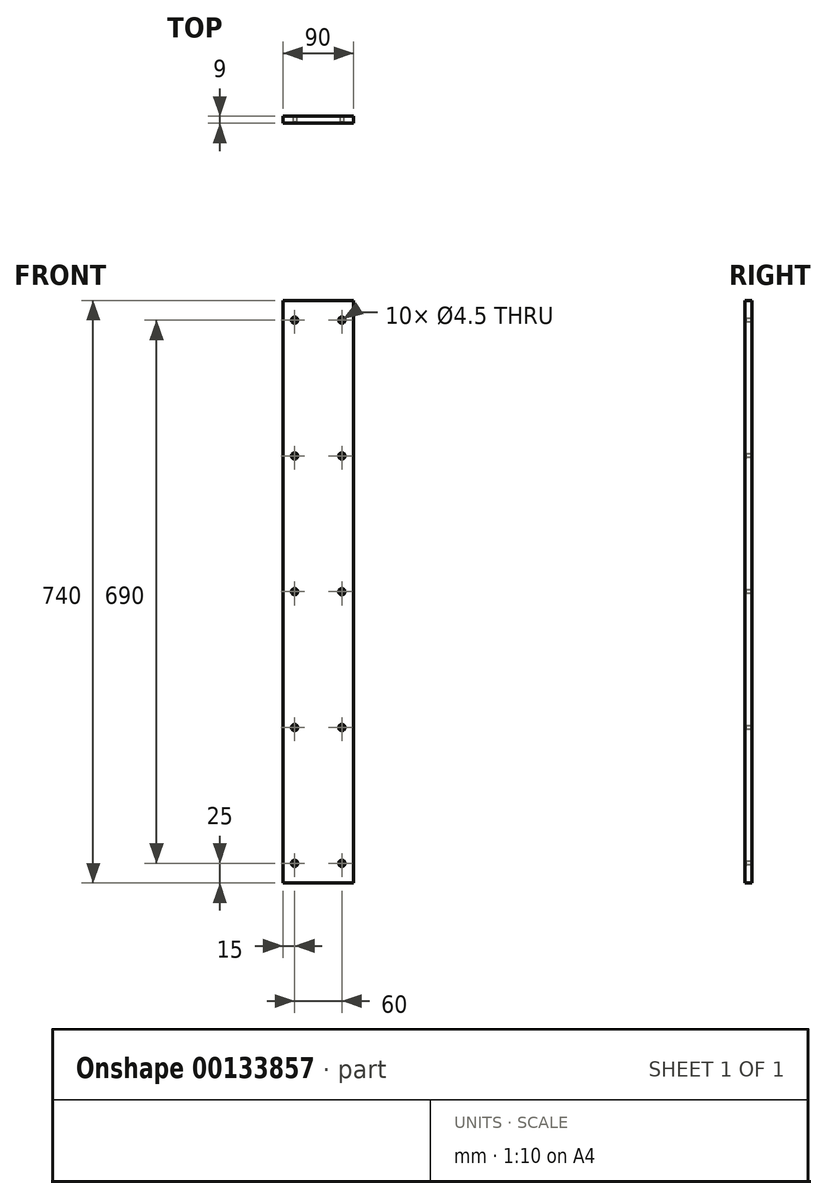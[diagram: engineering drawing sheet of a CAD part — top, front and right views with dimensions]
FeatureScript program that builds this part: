
annotation { "Feature Type Name" : "Feature", "Feature Type Description" : "" }
export const myFeature = defineFeature(function(context is Context, id is Id, definition is map)
    precondition{}
    {
        {
            var Q0;
            Q0=qCreatedBy(makeId("Top.planeOp"),FACE);
            var sketch = newSketch(context, id + "F0", { "sketchPlane" : qUnion([Q0])});
            skLineSegment(sketch, "E0.bottom", {"start": v(45, -4.5) * mm, "end": v(-45, -4.5) * mm});
            skLineSegment(sketch, "E0.top", {"start": v(45, 4.5) * mm, "end": v(-45, 4.5) * mm});
            skLineSegment(sketch, "E0.left", {"start": v(45, -4.5) * mm, "end": v(45, 4.5) * mm});
            skLineSegment(sketch, "E0.right", {"start": v(-45, -4.5) * mm, "end": v(-45, 4.5) * mm});
            skPoint(sketch, "E0.middle", {"position": v(0, 0) * mm});
            skSolve(sketch);
        }
        {
            var Q0;
            Q0=makeQuery(id+"F0.imprint","IMPRINT",FACE,{"disambiguationData":[TD([[makeQuery(id+"F0.imprint","IMPRINT",EDGE,{"derivedFrom":sQuery(id+"F0.wireOp",EDGE,"E0.bottom")}),-1.0]])]});
            extrude(context, id + "F1", {"entities" : qUnion([Q0]), "oppositeDirection" : true, "depth" : 740 * mm});
        }
        {
            var Q0;
            Q0=makeQuery(id+"F1.opExtrude","SWEPT_FACE",FACE,{"disambiguationData":[OSD([sQuery(id+"F0.wireOp",EDGE,"E0.bottom")])]});
            var sketch = newSketch(context, id + "F2", { "sketchPlane" : qUnion([Q0])});
            skPoint(sketch, "E1", {"position": v(-30, -25) * mm});
            skPoint(sketch, "E2", {"position": v(-30, -197.5) * mm});
            skPoint(sketch, "E3", {"position": v(-30, -370) * mm});
            skPoint(sketch, "E4", {"position": v(-30, -542.5) * mm});
            skPoint(sketch, "E5", {"position": v(-30, -715) * mm});
            skPoint(sketch, "E6", {"position": v(30, -715) * mm});
            skPoint(sketch, "E7", {"position": v(30, -542.5) * mm});
            skPoint(sketch, "E8", {"position": v(30, -370) * mm});
            skPoint(sketch, "E9", {"position": v(30, -197.5) * mm});
            skPoint(sketch, "E10", {"position": v(30, -25) * mm});
            skSolve(sketch);
        }
        {
            var Q0;
            Q0=sQuery(id+"F2.wireOp",VERTEX,"E5");
            var Q1;
            Q1=sQuery(id+"F2.wireOp",VERTEX,"E1");
            var Q2;
            Q2=sQuery(id+"F2.wireOp",VERTEX,"E4");
            var Q3;
            Q3=sQuery(id+"F2.wireOp",VERTEX,"E3");
            var Q4;
            Q4=sQuery(id+"F2.wireOp",VERTEX,"E2");
            var Q5;
            Q5=sQuery(id+"F2.wireOp",VERTEX,"E10");
            var Q6;
            Q6=sQuery(id+"F2.wireOp",VERTEX,"E9");
            var Q7;
            Q7=sQuery(id+"F2.wireOp",VERTEX,"E8");
            var Q8;
            Q8=sQuery(id+"F2.wireOp",VERTEX,"E7");
            var Q9;
            Q9=sQuery(id+"F2.wireOp",VERTEX,"E6");
            var Q10;
            Q10=makeQuery(id+"F1.opExtrude","SWEPT_BODY",BODY,{"disambiguationData":[OSD([sQuery(id+"F0.wireOp",EDGE,"E0.bottom"),sQuery(id+"F0.wireOp",EDGE,"E0.top"),sQuery(id+"F0.wireOp",EDGE,"E0.left"),sQuery(id+"F0.wireOp",EDGE,"E0.right")])]});
            hole(context, id + "F3", {"style" : HoleStyle.C_SINK, "endStyle" : HoleEndStyle.THROUGH, "holeDiameter" : 4.5 * mm, "cSinkDiameter" : 8 * mm, "cSinkAngle" : 90 * degree, "startFromSketch" : true, "locations" : qUnion([Q0, Q1, Q2, Q3, Q4, Q5, Q6, Q7, Q8, Q9]), "scope" : qUnion([Q10]), "isTappedThrough" : true});
        }
    });
